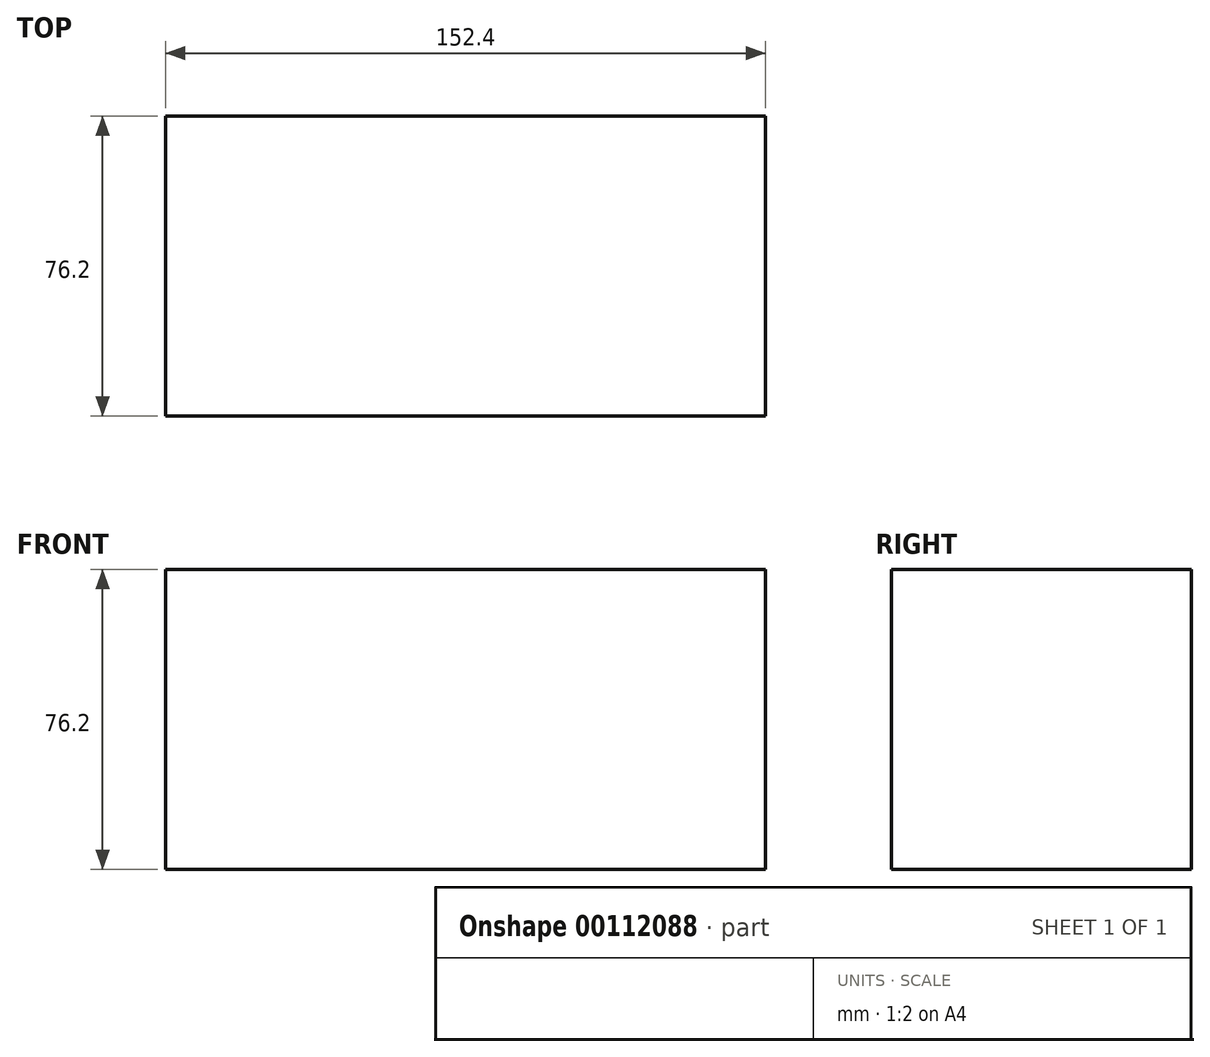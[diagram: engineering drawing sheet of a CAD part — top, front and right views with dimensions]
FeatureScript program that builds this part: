
annotation { "Feature Type Name" : "Feature", "Feature Type Description" : "" }
export const myFeature = defineFeature(function(context is Context, id is Id, definition is map)
    precondition{}
    {
        {
            var Q0;
            Q0=qCreatedBy(makeId("Top.planeOp"),FACE);
            var sketch = newSketch(context, id + "F0", { "sketchPlane" : qUnion([Q0])});
            skLineSegment(sketch, "E0.bottom", {"start": v(-76.2, 38.1) * mm, "end": v(76.2, 38.1) * mm});
            skLineSegment(sketch, "E0.top", {"start": v(-76.2, -38.1) * mm, "end": v(76.2, -38.1) * mm});
            skLineSegment(sketch, "E0.left", {"start": v(-76.2, 38.1) * mm, "end": v(-76.2, -38.1) * mm});
            skLineSegment(sketch, "E0.right", {"start": v(76.2, 38.1) * mm, "end": v(76.2, -38.1) * mm});
            skSolve(sketch);
        }
        {
            var Q0;
            Q0=makeQuery(id+"F0.imprint","IMPRINT",FACE,{"disambiguationData":[TD([[makeQuery(id+"F0.imprint","IMPRINT",EDGE,{"derivedFrom":sQuery(id+"F0.wireOp",EDGE,"E0.bottom")}),-1.0]])]});
            extrude(context, id + "F1", {"entities" : qUnion([Q0]), "depth" : 76.2 * mm});
        }
    });
